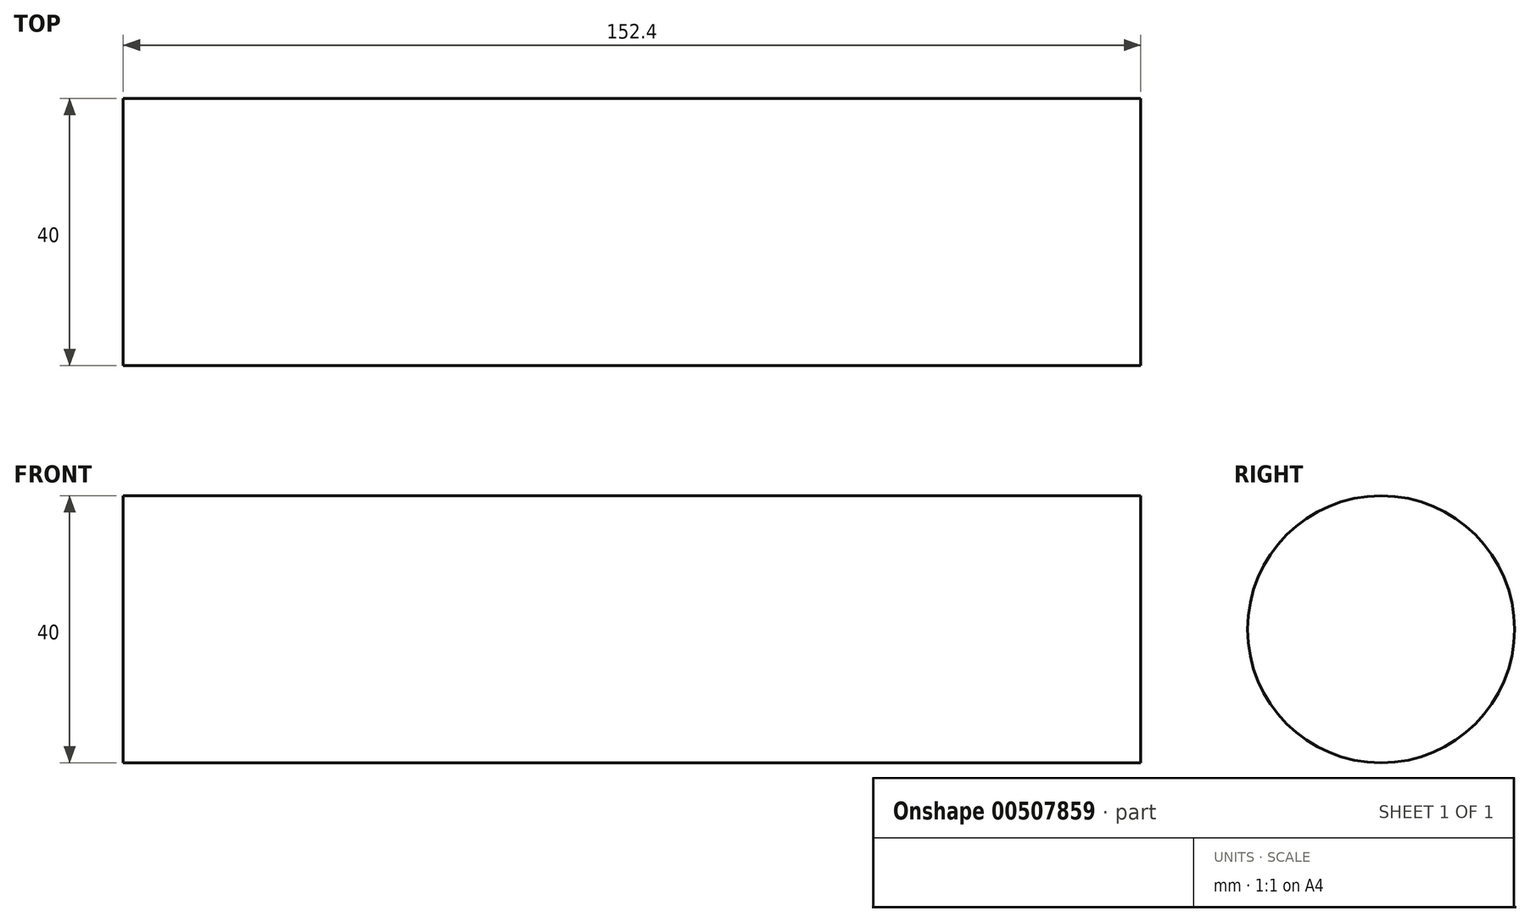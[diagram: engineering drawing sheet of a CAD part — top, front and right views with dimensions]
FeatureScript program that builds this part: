
annotation { "Feature Type Name" : "Feature", "Feature Type Description" : "" }
export const myFeature = defineFeature(function(context is Context, id is Id, definition is map)
    precondition{}
    {
        {
            var Q0;
            Q0=qCreatedBy(makeId("Right.planeOp"),FACE);
            var sketch = newSketch(context, id + "F0", { "sketchPlane" : qUnion([Q0])});
            skCircle(sketch, "E0", {"center": v(0, 0) * mm, "radius": 20 * mm});
            skSolve(sketch);
        }
        {
            var Q0;
            Q0 = qSketchRegion(id + "F0", true);
            extrude(context, id + "F1", {"entities" : qUnion([Q0]), "depth" : 152.4 * mm});
        }
    });
